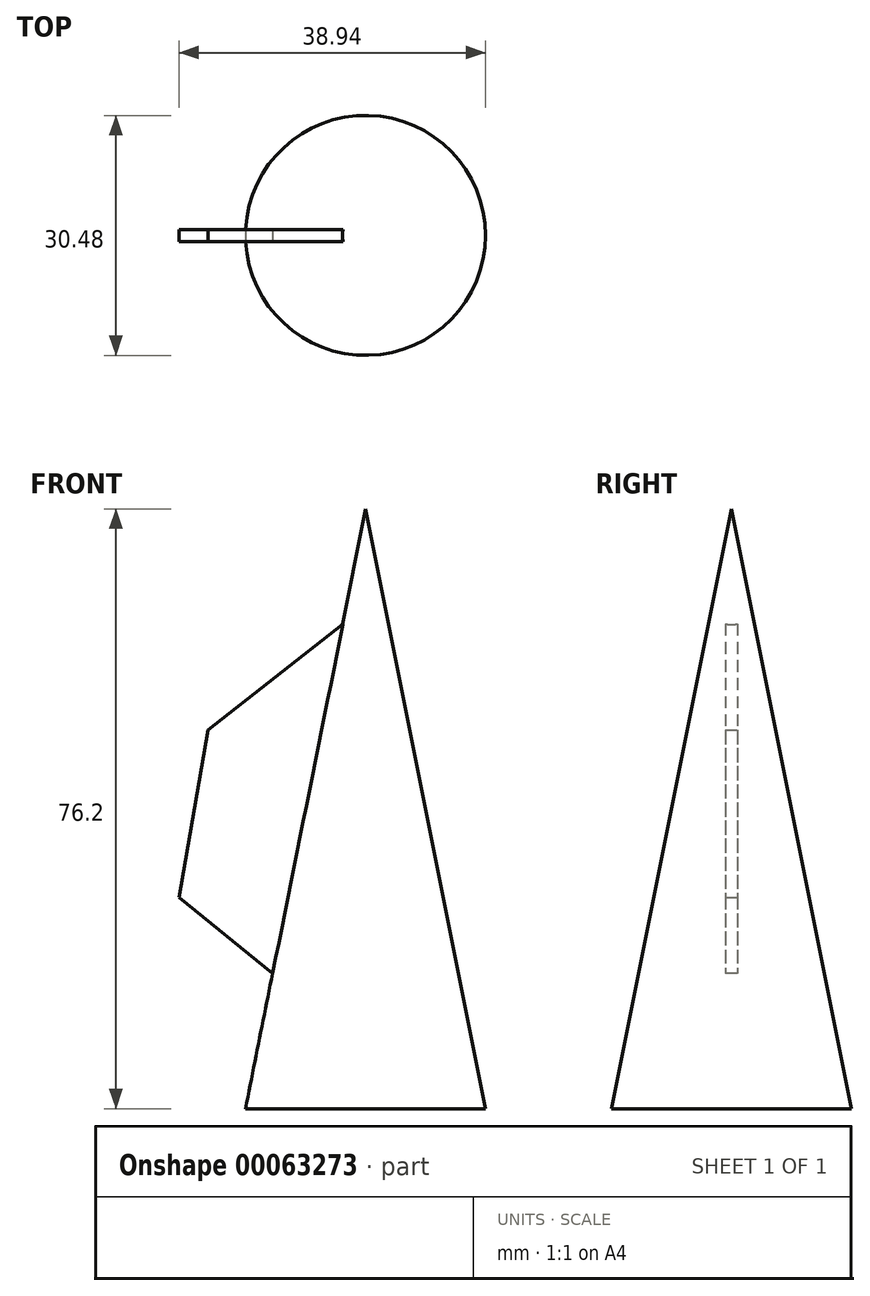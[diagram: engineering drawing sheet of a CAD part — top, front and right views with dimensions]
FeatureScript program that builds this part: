
annotation { "Feature Type Name" : "Feature", "Feature Type Description" : "" }
export const myFeature = defineFeature(function(context is Context, id is Id, definition is map)
    precondition{}
    {
        {
            var Q0;
            Q0=qCreatedBy(makeId("Front.planeOp"),FACE);
            var sketch = newSketch(context, id + "F0", { "sketchPlane" : qUnion([Q0])});
            skLineSegment(sketch, "E0", {"start": v(0, 0) * mm, "end": v(-15.24, 0) * mm});
            skLineSegment(sketch, "E1", {"start": v(-15.24, 0) * mm, "end": v(0, 76.2) * mm});
            skLineSegment(sketch, "E2", {"start": v(0, 76.2) * mm, "end": v(0, 0) * mm});
            skSolve(sketch);
        }
        {
            var Q0;
            Q0 = qSketchRegion(id + "F0", true);
            var Q1;
            Q1=sQuery(id+"F0.wireOp",EDGE,"E2");
            revolve(context, id + "F1", {"entities" : qUnion([Q0]), "axis" : qUnion([Q1]), "revolveType" : RevolveType.FULL});
        }
        {
            var Q0;
            Q0=qCreatedBy(makeId("Front.planeOp"),FACE);
            var sketch = newSketch(context, id + "F2", { "sketchPlane" : qUnion([Q0])});
            skLineSegment(sketch, "E3", {"start": v(0, 63.8) * mm, "end": v(-19.97, 48.1) * mm});
            skLineSegment(sketch, "E4", {"start": v(-19.97, 48.1) * mm, "end": v(-23.7, 26.84) * mm});
            skLineSegment(sketch, "E5", {"start": v(-23.7, 26.84) * mm, "end": v(0, 7.67) * mm});
            skLineSegment(sketch, "E6", {"start": v(0, 7.67) * mm, "end": v(0, 63.8) * mm});
            skSolve(sketch);
        }
        {
            var Q0;
            Q0=makeQuery(id+"F2.imprint","IMPRINT",FACE,{"disambiguationData":[TD([[makeQuery(id+"F2.imprint","IMPRINT",EDGE,{"derivedFrom":sQuery(id+"F2.wireOp",EDGE,"E3")}),1.0]])]});
            extrude(context, id + "F3", {"entities" : qUnion([Q0]), "operationType" : NewBodyOperationType.ADD, "depth" : 0.76 * mm, "hasSecondDirection" : true, "secondDirectionOppositeDirection" : true, "secondDirectionDepth" : 0.76 * mm});
        }
    });
